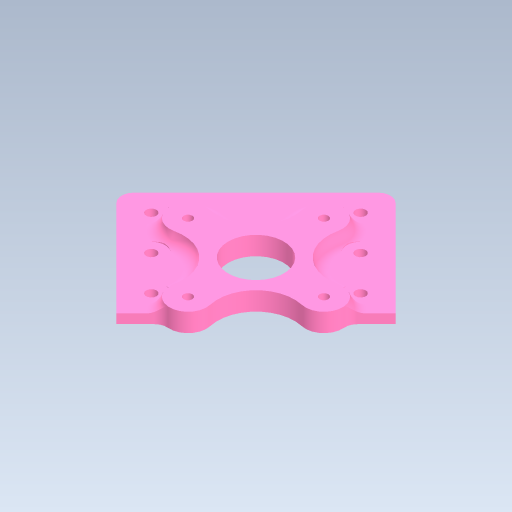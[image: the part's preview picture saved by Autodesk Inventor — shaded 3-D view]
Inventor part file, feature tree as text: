
AUTODESK INVENTOR PART (.ipt)
format: ipt  version: 2023 (Build 270158000, 158)  size: 316,416 bytes
history: native  units: in
note: dims shown in document units (in); Inventor stores cm internally (conversion verified against a paired STEP export)
features: sketch x4, extrude x4, projected_geometry x3, hole x1, fillet x1
ambient origin geometry x8: Origin, YZ Plane, XZ Plane, XY Plane, X Axis, Y Axis, Z Axis, Center Point
bodies: Solid1 (feature_tree)
feature tree (13):
  sketch  "Sketch1"  dims[d0=0.75in d1=1.5748in d3=360.0deg]
  extrude  "Extrusion1"  Depth=1.5748in TaperAngle=360.0deg
  hole  "Hole1"  [1 undecoded]
  extrude  "Extrusion2"  Depth=1.5748in TaperAngle=360.0deg
  fillet  "Fillet1"  Radius=0.375in
  extrude  "Extrusion3"  Depth=0.25in
  extrude  "Extrusion4"  Depth=0.25in
  sketch  "Sketch2"  dims[d5=1.378in d6=1.125in]
  projected_geometry  "Projected Loop1"
  sketch  "Sketch3"  dims[d7=1.625in d8=1.5748in d10=360.0deg d12=0.375in d13=0.0in]
  projected_geometry  "Projected Loop2"
  sketch  "Sketch4"  dims[d14=0.1772in d15=0.75in d16=0.2067in d17=0.1969in d18=0.5635in d19=1.0in d20=0.8108in d21=0.5in d22=4.0in d23=3.0in d24=0.5in d25=45.0deg d26=1.1811in d28=1.0in d29=0.7874in d31=3.0in d34=3.0in d35=1.125in d36=0.2087in d37=0.1875in d38=0.0in d39=0.25in d40=0.56in d41=0.56in d42=0.56in d43=0.56in d44=0.56in d45=0.56in d46=0.1875in d47=0.0in d49=0.0625in d50=0.0in d51=0.5in d52=0.125in]
  projected_geometry  "Projected Loop3"
note: 1 required parameter value undecoded (feature->parameter linkage not recoverable at this tier; creation-order binding heuristic only, values carry confidence <= 0.55)
